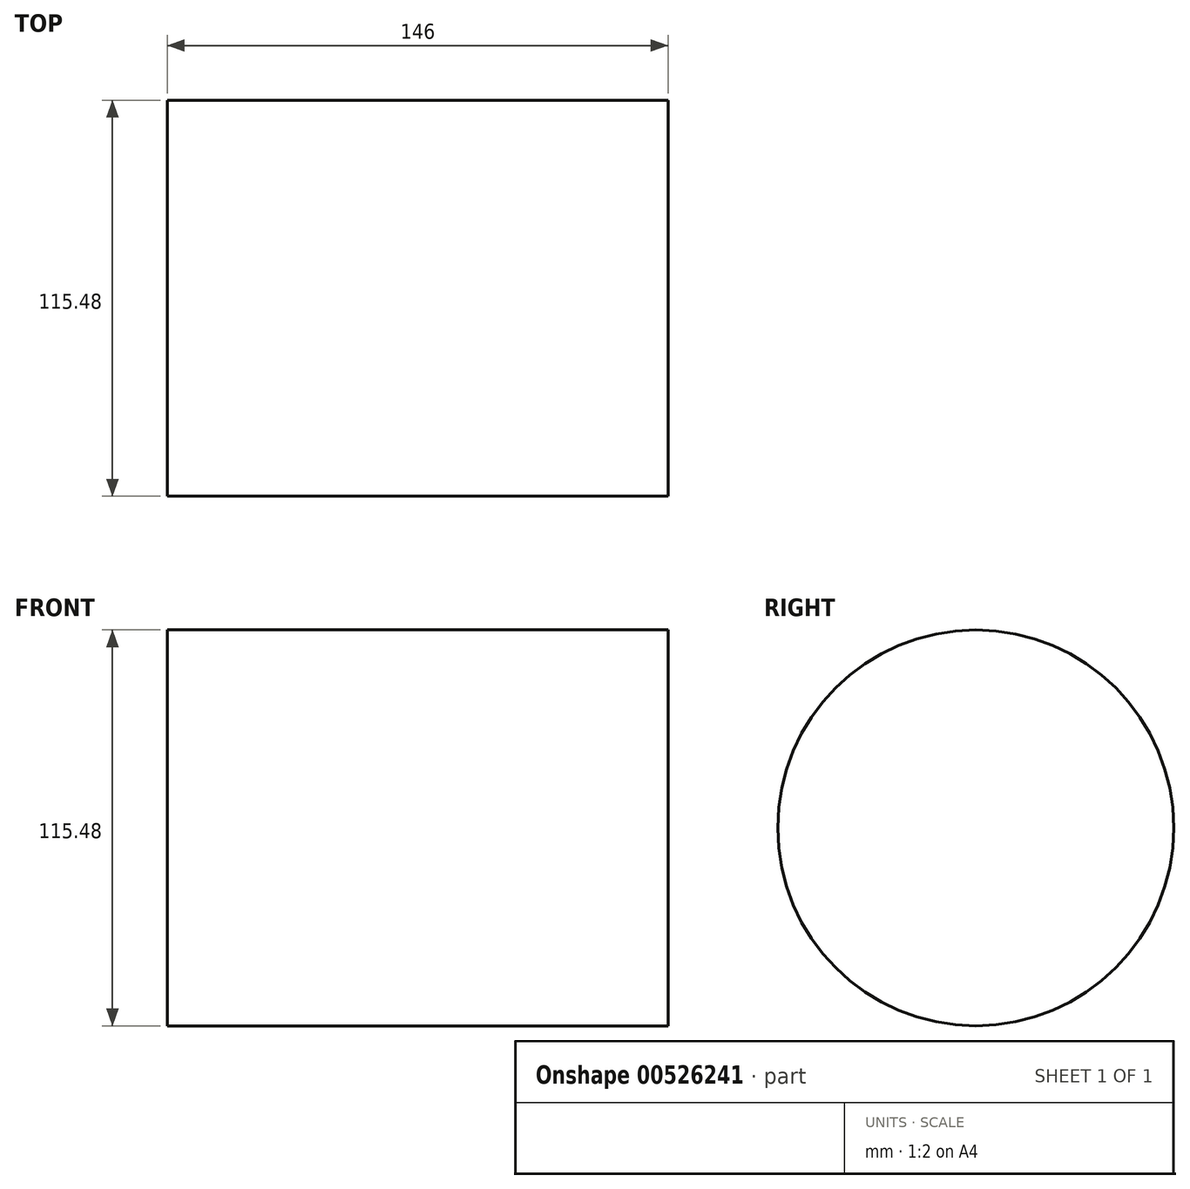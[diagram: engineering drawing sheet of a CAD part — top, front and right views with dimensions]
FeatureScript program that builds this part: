
annotation { "Feature Type Name" : "Feature", "Feature Type Description" : "" }
export const myFeature = defineFeature(function(context is Context, id is Id, definition is map)
    precondition{}
    {
        {
            var Q0;
            Q0=qCreatedBy(makeId("Right.planeOp"),FACE);
            var sketch = newSketch(context, id + "F0", { "sketchPlane" : qUnion([Q0])});
            skCircle(sketch, "E0", {"center": v(-155.6, 100.95) * mm, "radius": 57.74 * mm});
            skSolve(sketch);
        }
        {
            var Q0;
            Q0=makeQuery(id+"F0.imprint","IMPRINT",FACE,{"disambiguationData":[TD([[makeQuery(id+"F0.imprint","IMPRINT",EDGE,{"derivedFrom":sQuery(id+"F0.wireOp",EDGE,"E0")}),1.0]])]});
            extrude(context, id + "F1", {"entities" : qUnion([Q0]), "depth" : 146 * mm, "offsetDistance" : 25 * mm});
        }
    });
